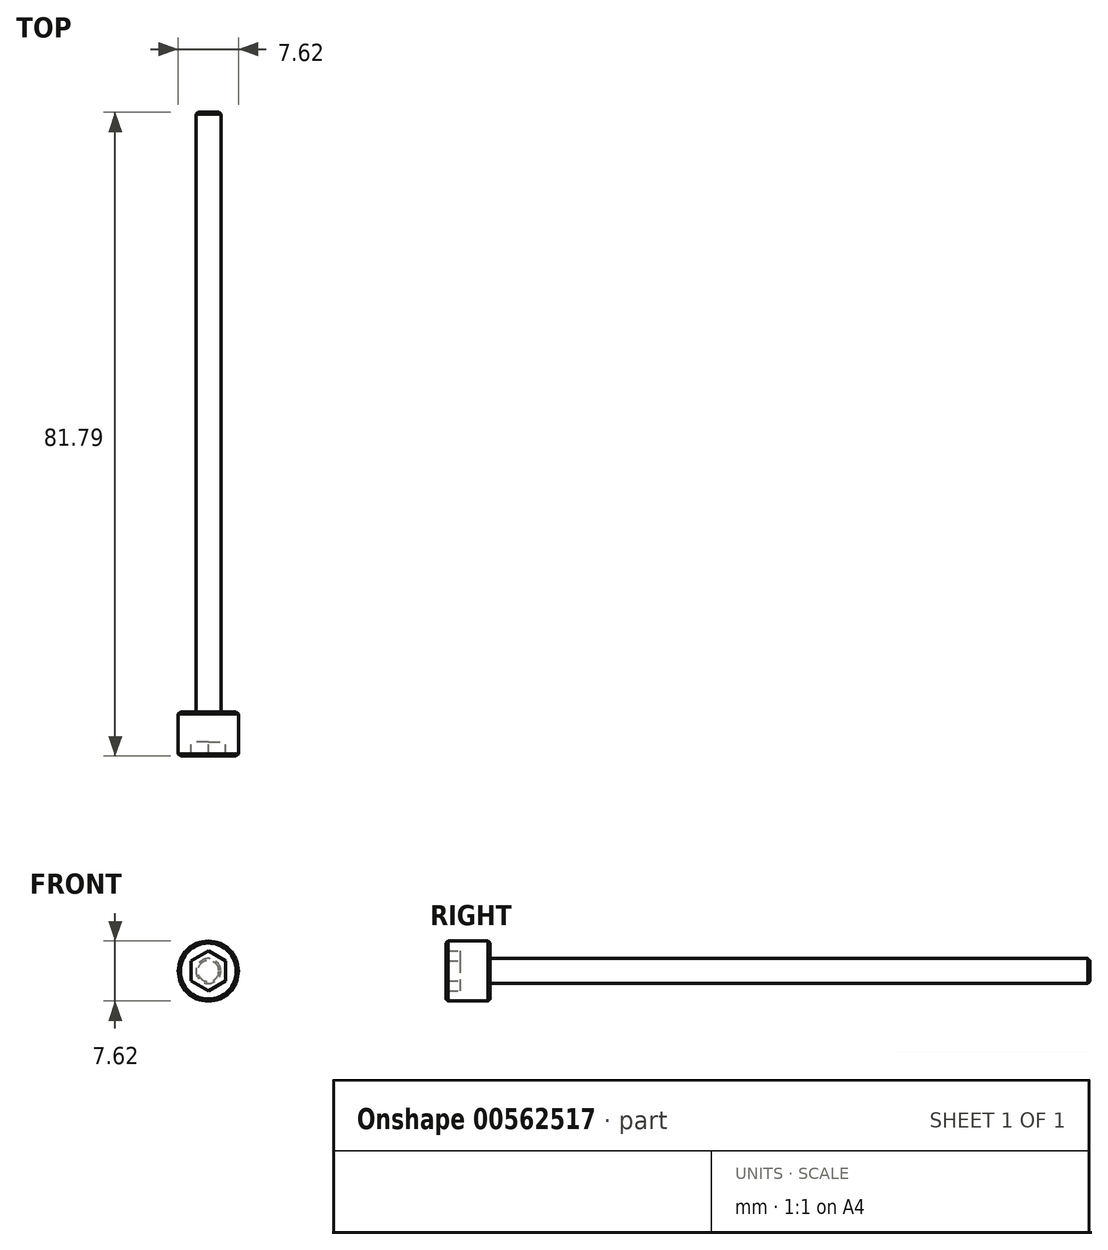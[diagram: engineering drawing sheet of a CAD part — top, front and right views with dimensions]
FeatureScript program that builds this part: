
annotation { "Feature Type Name" : "Feature", "Feature Type Description" : "" }
export const myFeature = defineFeature(function(context is Context, id is Id, definition is map)
    precondition{}
    {
        {
            var Q0;
            Q0=qCreatedBy(makeId("Front.planeOp"),FACE);
            var sketch = newSketch(context, id + "F0", { "sketchPlane" : qUnion([Q0])});
            skCircle(sketch, "E0.cCircle", {"center": v(0, 0) * mm, "radius": 2.2 * mm, "construction": true});
            skLineSegment(sketch, "E0.0", {"start": v(2.2, 1.27) * mm, "end": v(2.2, -1.27) * mm});
            skLineSegment(sketch, "E0.1", {"start": v(2.2, -1.27) * mm, "end": v(0, -2.54) * mm});
            skLineSegment(sketch, "E0.2", {"start": v(0, -2.54) * mm, "end": v(-2.2, -1.27) * mm});
            skLineSegment(sketch, "E0.3", {"start": v(-2.2, -1.27) * mm, "end": v(-2.2, 1.27) * mm});
            skLineSegment(sketch, "E0.4", {"start": v(-2.2, 1.27) * mm, "end": v(0, 2.54) * mm});
            skLineSegment(sketch, "E0.5", {"start": v(0, 2.54) * mm, "end": v(2.2, 1.27) * mm});
            skPoint(sketch, "E0.0.midPoint", {"position": v(2.2, 0) * mm});
            skCircle(sketch, "E1", {"center": v(0, 0) * mm, "radius": 3.81 * mm});
            skSolve(sketch);
        }
        {
            var Q0;
            Q0=qSketchRegion(id+"F0",true);
            extrude(context, id + "F1", {"entities" : qUnion([Q0]), "depth" : 5.6 * mm, "offsetDistance" : 25.4 * mm});
        }
        {
            var Q0;
            Q0=makeQuery(id+"F0.imprint","IMPRINT",FACE,{"disambiguationData":[TD([[makeQuery(id+"F0.imprint","IMPRINT",EDGE,{"derivedFrom":sQuery(id+"F0.wireOp",EDGE,"E0.0")}),-1.0]])]});
            extrude(context, id + "F2", {"entities" : qUnion([Q0]), "operationType" : NewBodyOperationType.ADD, "depth" : 3.8 * mm, "offsetDistance" : 25.4 * mm});
        }
        {
            var Q0;
            {var subQ0=sQuery(id+"F0.wireOp",EDGE,"E0.5");var subQ1=sQuery(id+"F0.wireOp",EDGE,"E0.4");var subQ2=sQuery(id+"F0.wireOp",EDGE,"E0.3");var subQ3=sQuery(id+"F0.wireOp",EDGE,"E0.2");var subQ4=sQuery(id+"F0.wireOp",EDGE,"E0.1");var subQ5=sQuery(id+"F0.wireOp",EDGE,"E0.0");Q0=makeQuery(id+"F2.boolean.opBoolean","MERGE",FACE,{"derivedFrom":[makeQuery(id+"F1.opExtrude","CAP_FACE",FACE,{"disambiguationData":[OSD([subQ5,subQ4,subQ3,subQ2,subQ1,subQ0,sQuery(id+"F0.wireOp",EDGE,"E1")])],"isStart":true}),makeQuery(id+"F2.opExtrude","CAP_FACE",FACE,{"disambiguationData":[OSD([subQ5,subQ4,subQ3,subQ2,subQ1,subQ0])],"isStart":true})]});}
            var sketch = newSketch(context, id + "F3", { "sketchPlane" : qUnion([Q0])});
            skCircle(sketch, "E2", {"center": v(0, 0) * mm, "radius": 1.59 * mm});
            skSolve(sketch);
        }
        {
            var Q0;
            Q0=makeQuery(id+"F3.imprint","IMPRINT",FACE,{"disambiguationData":[TD([[makeQuery(id+"F3.imprint","IMPRINT",EDGE,{"derivedFrom":sQuery(id+"F3.wireOp",EDGE,"E2")}),1.0]])]});
            extrude(context, id + "F4", {"entities" : qUnion([Q0]), "operationType" : NewBodyOperationType.ADD, "depth" : 76.2 * mm, "offsetDistance" : 25.4 * mm});
        }
        {
            var Q0;
            Q0=makeQuery(id+"F1.opExtrude","CAP_EDGE",EDGE,{"disambiguationData":[OSD([sQuery(id+"F0.wireOp",EDGE,"E1")])],"isStart":false});
            var Q1;
            Q1=makeQuery(id+"F1.opExtrude","CAP_EDGE",EDGE,{"disambiguationData":[OSD([sQuery(id+"F0.wireOp",EDGE,"E1")])],"isStart":true});
            chamfer(context, id + "F5", {"entities" : qUnion([Q0, Q1]), "width" : 0.25 * mm, "tangentPropagation" : true});
        }
        {
            var Q0;
            Q0=makeQuery(id+"F4.opExtrude","CAP_EDGE",EDGE,{"disambiguationData":[OSD([sQuery(id+"F3.wireOp",EDGE,"E2")])],"isStart":false});
            chamfer(context, id + "F6", {"entities" : qUnion([Q0]), "width" : 0.25 * mm, "tangentPropagation" : true});
        }
    });
